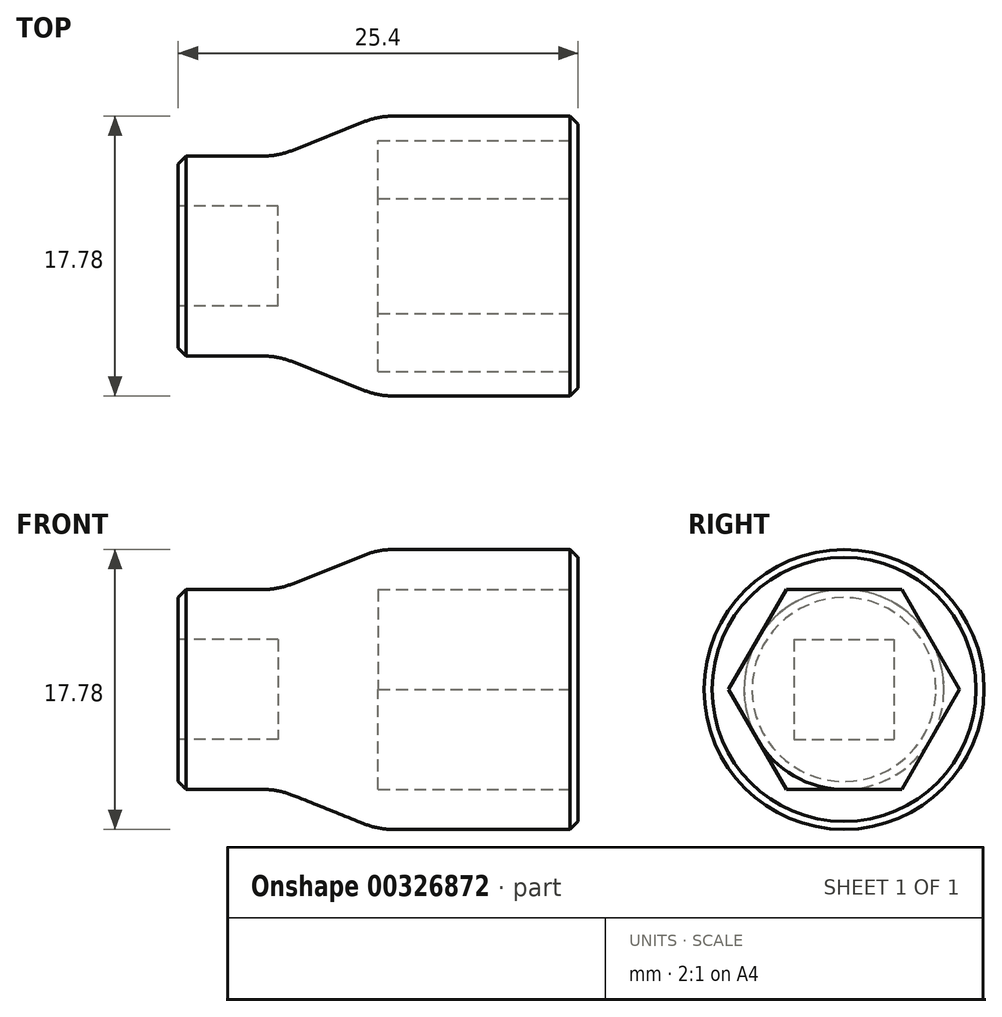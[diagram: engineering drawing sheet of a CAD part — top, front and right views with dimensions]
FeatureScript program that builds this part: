
annotation { "Feature Type Name" : "Feature", "Feature Type Description" : "" }
export const myFeature = defineFeature(function(context is Context, id is Id, definition is map)
    precondition{}
    {
        {
            var Q0;
            Q0=qCreatedBy(makeId("Top.planeOp"),FACE);
            var sketch = newSketch(context, id + "F0", { "sketchPlane" : qUnion([Q0])});
            skLineSegment(sketch, "E0", {"start": v(0, 0) * mm, "end": v(0, 6.35) * mm});
            skLineSegment(sketch, "E1", {"start": v(0, 6.35) * mm, "end": v(6.35, 6.35) * mm});
            skLineSegment(sketch, "E2", {"start": v(6.35, 6.35) * mm, "end": v(12.7, 8.9) * mm});
            skLineSegment(sketch, "E3", {"start": v(12.7, 8.9) * mm, "end": v(25.4, 8.9) * mm});
            skLineSegment(sketch, "E4", {"start": v(25.4, 8.9) * mm, "end": v(25.4, 0) * mm});
            skLineSegment(sketch, "E5", {"start": v(25.4, 0) * mm, "end": v(0, 0) * mm});
            skLineSegment(sketch, "E6", {"start": v(0, 0) * mm, "end": v(-6.6, 0) * mm, "construction": true});
            skSolve(sketch);
        }
        {
            var Q0;
            Q0 = qSketchRegion(id + "F0", true);
            var Q1;
            Q1=sQuery(id+"F0.wireOp",EDGE,"E6");
            revolve(context, id + "F1", {"entities" : qUnion([Q0]), "axis" : qUnion([Q1]), "revolveType" : RevolveType.FULL});
        }
        {
            var Q0;
            Q0=makeQuery(id+"F1.opRevolve","SWEPT_FACE",FACE,{"disambiguationData":[OSD([sQuery(id+"F0.wireOp",EDGE,"E0")])]});
            var sketch = newSketch(context, id + "F2", { "sketchPlane" : qUnion([Q0])});
            skLineSegment(sketch, "E7.bottom", {"start": v(3.17, 3.18) * mm, "end": v(-3.18, 3.18) * mm});
            skLineSegment(sketch, "E7.top", {"start": v(3.18, -3.18) * mm, "end": v(-3.17, -3.18) * mm});
            skLineSegment(sketch, "E7.left", {"start": v(3.17, 3.18) * mm, "end": v(3.18, -3.18) * mm});
            skLineSegment(sketch, "E7.right", {"start": v(-3.18, 3.18) * mm, "end": v(-3.17, -3.18) * mm});
            skPoint(sketch, "E7.middle", {"position": v(0, 0) * mm});
            skSolve(sketch);
        }
        {
            var Q0;
            Q0 = qSketchRegion(id + "F2", true);
            extrude(context, id + "F3", {"entities" : qUnion([Q0]), "operationType" : NewBodyOperationType.REMOVE, "oppositeDirection" : true, "depth" : 6.35 * mm});
        }
        {
            var Q0;
            Q0=makeQuery(id+"F1.opRevolve","SWEPT_FACE",FACE,{"disambiguationData":[OSD([sQuery(id+"F0.wireOp",EDGE,"E4")])]});
            var sketch = newSketch(context, id + "F4", { "sketchPlane" : qUnion([Q0])});
            skCircle(sketch, "E8.cCircle", {"center": v(0, 0) * mm, "radius": 6.35 * mm, "construction": true});
            skLineSegment(sketch, "E8.0", {"start": v(3.67, 6.35) * mm, "end": v(7.33, 0) * mm});
            skLineSegment(sketch, "E8.1", {"start": v(7.33, 0) * mm, "end": v(3.67, -6.35) * mm});
            skLineSegment(sketch, "E8.2", {"start": v(3.67, -6.35) * mm, "end": v(-3.67, -6.35) * mm});
            skLineSegment(sketch, "E8.3", {"start": v(-3.67, -6.35) * mm, "end": v(-7.33, 0) * mm});
            skLineSegment(sketch, "E8.4", {"start": v(-7.33, 0) * mm, "end": v(-3.67, 6.35) * mm});
            skLineSegment(sketch, "E8.5", {"start": v(-3.67, 6.35) * mm, "end": v(3.67, 6.35) * mm});
            skPoint(sketch, "E8.0.midPoint", {"position": v(5.5, 3.18) * mm});
            skSolve(sketch);
        }
        {
            var Q0;
            Q0 = qSketchRegion(id + "F4", true);
            extrude(context, id + "F5", {"entities" : qUnion([Q0]), "operationType" : NewBodyOperationType.REMOVE, "oppositeDirection" : true, "depth" : 12.7 * mm});
        }
        {
            var Q0;
            Q0=makeQuery(id+"F1.opRevolve","SWEPT_EDGE",EDGE,{"disambiguationData":[OSD([sQuery(id+"F0.wireOp",EDGE,"E2"),sQuery(id+"F0.wireOp",EDGE,"E3")])]});
            var Q1;
            Q1=makeQuery(id+"F1.opRevolve","SWEPT_EDGE",EDGE,{"disambiguationData":[OSD([sQuery(id+"F0.wireOp",EDGE,"E1"),sQuery(id+"F0.wireOp",EDGE,"E2")])]});
            fillet(context, id + "F6", {"entities" : qUnion([Q0, Q1]), "radius" : 5.08 * mm, "tangentPropagation" : true, "allowEdgeOverflow" : false});
        }
        {
            var Q0;
            Q0=makeQuery(id+"F1.opRevolve","SWEPT_EDGE",EDGE,{"disambiguationData":[OSD([sQuery(id+"F0.wireOp",EDGE,"E3"),sQuery(id+"F0.wireOp",EDGE,"E4")])]});
            var Q1;
            Q1=makeQuery(id+"F1.opRevolve","SWEPT_EDGE",EDGE,{"disambiguationData":[OSD([sQuery(id+"F0.wireOp",EDGE,"E0"),sQuery(id+"F0.wireOp",EDGE,"E1")])]});
            chamfer(context, id + "F7", {"entities" : qUnion([Q0, Q1]), "width" : 0.5 * mm, "tangentPropagation" : true});
        }
    });
